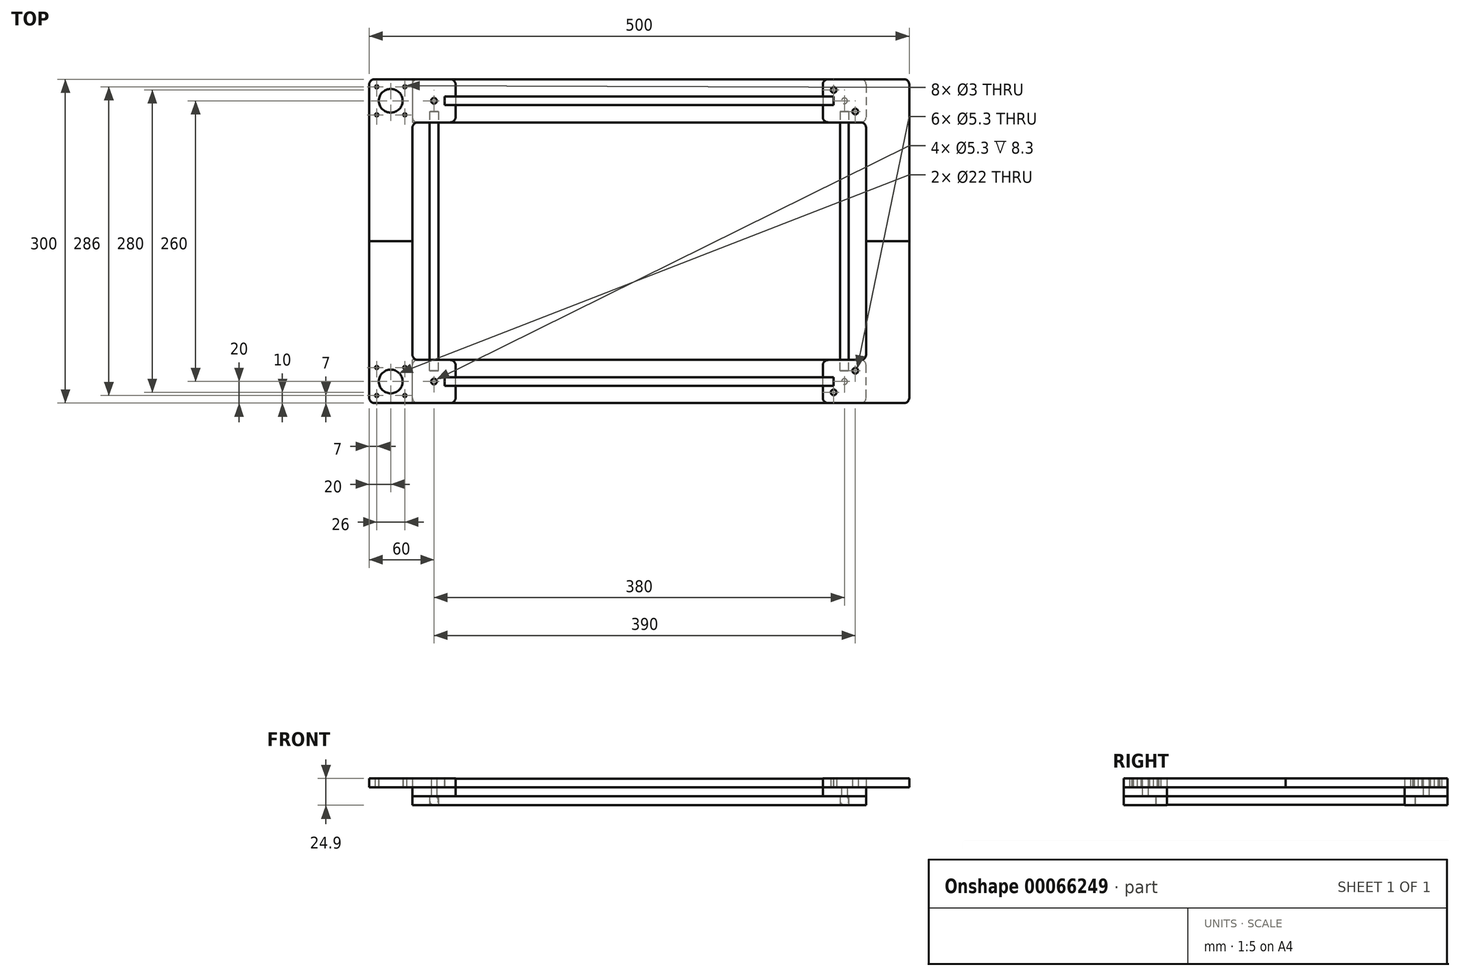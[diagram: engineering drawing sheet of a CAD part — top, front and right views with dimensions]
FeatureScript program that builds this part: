
annotation { "Feature Type Name" : "Feature", "Feature Type Description" : "" }
export const myFeature = defineFeature(function(context is Context, id is Id, definition is map)
    precondition{}
    {
        {
            assignVariable(context, id + "F0", {"name" : "thickness", "anyValue" : 8.3});
        }
        {
            var Q0;
            Q0=qCreatedBy(makeId("Top.planeOp"),FACE);
            var sketch = newSketch(context, id + "F1", { "sketchPlane" : qUnion([Q0])});
            skLineSegment(sketch, "E0.rect.bottom", {"start": v(170, -105) * mm, "end": v(-170, -105) * mm, "construction": true});
            skLineSegment(sketch, "E0.rect.top", {"start": v(170, 105) * mm, "end": v(-170, 105) * mm, "construction": true});
            skLineSegment(sketch, "E0.rect.left", {"start": v(170, -105) * mm, "end": v(170, 105) * mm, "construction": true});
            skLineSegment(sketch, "E0.rect.right", {"start": v(-170, -105) * mm, "end": v(-170, 105) * mm, "construction": true});
            skPoint(sketch, "E0.rect.middle", {"position": v(0, 0) * mm});
            skLineSegment(sketch, "E1.rect.bottom", {"start": v(250, -150) * mm, "end": v(-250, -150) * mm, "construction": true});
            skLineSegment(sketch, "E1.rect.top", {"start": v(250, 150) * mm, "end": v(-250, 150) * mm, "construction": true});
            skLineSegment(sketch, "E1.rect.left", {"start": v(250, -150) * mm, "end": v(250, 150) * mm, "construction": true});
            skLineSegment(sketch, "E1.rect.right", {"start": v(-250, -150) * mm, "end": v(-250, 150) * mm, "construction": true});
            skPoint(sketch, "E2.firstSnap0", {"position": v(170, 0) * mm});
            skLineSegment(sketch, "E2.bottom", {"start": v(170, 150) * mm, "end": v(250, 150) * mm, "construction": true});
            skLineSegment(sketch, "E2.top", {"start": v(170, -150) * mm, "end": v(250, -150) * mm, "construction": true});
            skLineSegment(sketch, "E2.left", {"start": v(170, 150) * mm, "end": v(170, -150) * mm, "construction": true});
            skLineSegment(sketch, "E2.right", {"start": v(250, 150) * mm, "end": v(250, -150) * mm, "construction": true});
            skLineSegment(sketch, "E3.bottom", {"start": v(-250, 150) * mm, "end": v(-170, 150) * mm, "construction": true});
            skLineSegment(sketch, "E3.top", {"start": v(-250, -150) * mm, "end": v(-170, -150) * mm, "construction": true});
            skLineSegment(sketch, "E3.left", {"start": v(-250, 150) * mm, "end": v(-250, -150) * mm, "construction": true});
            skLineSegment(sketch, "E3.right", {"start": v(-170, 150) * mm, "end": v(-170, -150) * mm, "construction": true});
            skPoint(sketch, "E4.rect.middle.positionSnap0", {"position": v(0, 105) * mm});
            skPoint(sketch, "E4.rect.centerSnap0", {"position": v(0, 105) * mm});
            skLineSegment(sketch, "E5.rect.bottom", {"start": v(-295.27, -46.95) * mm, "end": v(-355.57, -46.95) * mm, "construction": true});
            skLineSegment(sketch, "E5.rect.top", {"start": v(-295.27, 54.65) * mm, "end": v(-355.57, 54.65) * mm, "construction": true});
            skLineSegment(sketch, "E5.rect.left", {"start": v(-295.27, -46.95) * mm, "end": v(-295.27, 54.65) * mm, "construction": true});
            skLineSegment(sketch, "E5.rect.right", {"start": v(-355.57, -46.95) * mm, "end": v(-355.57, 54.65) * mm, "construction": true});
            skPoint(sketch, "E5.rect.middle.positionSnap0", {"position": v(-170, 0) * mm});
            skPoint(sketch, "E5.rect.centerSnap0", {"position": v(-170, 0) * mm});
            skLineSegment(sketch, "E6", {"start": v(-170, 0) * mm, "end": v(0, 0) * mm, "construction": true});
            skLineSegment(sketch, "E7.rect.top", {"start": v(-186, 0) * mm, "end": v(-194, 0) * mm, "construction": true});
            skLineSegment(sketch, "E7.rect.right", {"start": v(-194, 120) * mm, "end": v(-194, 0) * mm, "construction": true});
            skLineSegment(sketch, "E8", {"start": v(0, 0) * mm, "end": v(0, 105) * mm, "construction": true});
            skLineSegment(sketch, "E9.bottom", {"start": v(-180, 134) * mm, "end": v(0, 134) * mm, "construction": true});
            skLineSegment(sketch, "E9.top", {"start": v(-180, 126) * mm, "end": v(0, 126) * mm, "construction": true});
            skLineSegment(sketch, "E9.right", {"start": v(0, 134) * mm, "end": v(0, 126) * mm, "construction": true});
            skLineSegment(sketch, "E10.rect.bottom", {"start": v(-212.5, 112.5) * mm, "end": v(-247.5, 112.5) * mm, "construction": true});
            skLineSegment(sketch, "E10.rect.top", {"start": v(-212.5, 147.5) * mm, "end": v(-247.5, 147.5) * mm, "construction": true});
            skLineSegment(sketch, "E10.rect.left", {"start": v(-212.5, 112.5) * mm, "end": v(-212.5, 147.5) * mm, "construction": true});
            skLineSegment(sketch, "E10.rect.right", {"start": v(-247.5, 112.5) * mm, "end": v(-247.5, 147.5) * mm, "construction": true});
            skPoint(sketch, "E10.rect.middle", {"position": v(-230, 130) * mm});
            skLineSegment(sketch, "E11.rect.bottom", {"start": v(-217, 117) * mm, "end": v(-243, 117) * mm, "construction": true});
            skLineSegment(sketch, "E11.rect.top", {"start": v(-217, 143) * mm, "end": v(-243, 143) * mm, "construction": true});
            skLineSegment(sketch, "E11.rect.left", {"start": v(-217, 117) * mm, "end": v(-217, 143) * mm, "construction": true});
            skLineSegment(sketch, "E11.rect.right", {"start": v(-243, 117) * mm, "end": v(-243, 143) * mm, "construction": true});
            skCircle(sketch, "E12", {"center": v(-243, 143) * mm, "radius": 1.5 * mm, "construction": true});
            skCircle(sketch, "E13", {"center": v(-217, 143) * mm, "radius": 1.5 * mm, "construction": true});
            skCircle(sketch, "E14", {"center": v(-243, 117) * mm, "radius": 1.5 * mm, "construction": true});
            skCircle(sketch, "E15", {"center": v(-217, 117) * mm, "radius": 1.5 * mm, "construction": true});
            skLineSegment(sketch, "E16", {"start": v(-190, 130) * mm, "end": v(-180, 120) * mm, "construction": true});
            skLineSegment(sketch, "E17", {"start": v(-194, 120) * mm, "end": v(-186, 120) * mm, "construction": true});
            skLineSegment(sketch, "E18.trimOffspring", {"start": v(-186, 120) * mm, "end": v(-186, 0) * mm, "construction": true});
            skLineSegment(sketch, "E19", {"start": v(-180, 134) * mm, "end": v(-180, 126) * mm, "construction": true});
            skPoint(sketch, "E20", {"position": v(-190, 120) * mm});
            skPoint(sketch, "E21", {"position": v(-180, 130) * mm});
            skPoint(sketch, "E22", {"position": v(-190, 130) * mm});
            skLineSegment(sketch, "E23.top", {"start": v(-170, 110) * mm, "end": v(-210, 110) * mm, "construction": true});
            skLineSegment(sketch, "E23.left", {"start": v(-170, 150) * mm, "end": v(-170, 110) * mm, "construction": true});
            skLineSegment(sketch, "E23.right", {"start": v(-210, 150) * mm, "end": v(-210, 110) * mm, "construction": true});
            skLineSegment(sketch, "E24", {"start": v(-210, 150) * mm, "end": v(-170, 150) * mm});
            skLineSegment(sketch, "E25", {"start": v(-170, 110) * mm, "end": v(210, 110) * mm, "construction": true});
            skLineSegment(sketch, "E26", {"start": v(210, 110) * mm, "end": v(210, -110) * mm, "construction": true});
            skPoint(sketch, "E27.orphan", {"position": v(170, 110) * mm});
            skLineSegment(sketch, "E28.MirrorCS", {"start": v(-170, -110) * mm, "end": v(210, -110) * mm, "construction": true});
            skPoint(sketch, "E29.orphan", {"position": v(210, 0) * mm});
            skLineSegment(sketch, "E30", {"start": v(127, 105) * mm, "end": v(127, -105) * mm, "construction": true});
            skCircle(sketch, "E31", {"center": v(-190, 130) * mm, "radius": 2.65 * mm});
            skSolve(sketch);
        }
        {
            var Q0;
            Q0=qCreatedBy(makeId("Top.planeOp"),FACE);
            var sketch = newSketch(context, id + "F2", { "sketchPlane" : qUnion([Q0])});
            skLineSegment(sketch, "E32.0", {"start": v(-250, 0) * mm, "end": v(-250, 150) * mm});
            skLineSegment(sketch, "E33.0", {"start": v(-250, 150) * mm, "end": v(-170, 150) * mm});
            skLineSegment(sketch, "E34", {"start": v(-170, 150) * mm, "end": v(-170, 134) * mm});
            skLineSegment(sketch, "E35.0", {"start": v(-250, 0) * mm, "end": v(-210, 0) * mm});
            skLineSegment(sketch, "E36", {"start": v(-210, 110) * mm, "end": v(-210, 0) * mm});
            skLineSegment(sketch, "E37.trimOffspring", {"start": v(-170, 110) * mm, "end": v(-210, 110) * mm});
            skLineSegment(sketch, "E38.0", {"start": v(-180, 134) * mm, "end": v(-170, 134) * mm});
            skLineSegment(sketch, "E39.0", {"start": v(-180, 126) * mm, "end": v(-170, 126) * mm});
            skLineSegment(sketch, "E40.0", {"start": v(-180, 134) * mm, "end": v(-180, 126) * mm});
            skPoint(sketch, "E41.orphan", {"position": v(0, 134) * mm});
            skPoint(sketch, "E42.orphan", {"position": v(0, 126) * mm});
            skLineSegment(sketch, "E43.trimOffspring", {"start": v(-170, 126) * mm, "end": v(-170, 110) * mm});
            skLineSegment(sketch, "E44", {"start": v(0, 0) * mm, "end": v(0, 126) * mm, "construction": true});
            skLineSegment(sketch, "E45.MirrorCS", {"start": v(180, 126) * mm, "end": v(170, 126) * mm});
            skLineSegment(sketch, "E46.MirrorCS", {"start": v(180, 134) * mm, "end": v(180, 126) * mm});
            skLineSegment(sketch, "E47.MirrorCS", {"start": v(180, 134) * mm, "end": v(170, 134) * mm});
            skLineSegment(sketch, "E48.MirrorCS", {"start": v(170, 150) * mm, "end": v(170, 134) * mm});
            skLineSegment(sketch, "E49.MirrorCS", {"start": v(170, 126) * mm, "end": v(170, 110) * mm});
            skLineSegment(sketch, "E50.MirrorCS", {"start": v(170, 110) * mm, "end": v(210, 110) * mm});
            skLineSegment(sketch, "E51.MirrorCS", {"start": v(250, 150) * mm, "end": v(170, 150) * mm});
            skLineSegment(sketch, "E52.0", {"start": v(210, 110) * mm, "end": v(210, 0) * mm});
            skLineSegment(sketch, "E53", {"start": v(210, 0) * mm, "end": v(250, 0) * mm});
            skLineSegment(sketch, "E54.0", {"start": v(250, 150) * mm, "end": v(250, 0) * mm});
            skCircle(sketch, "E55.MirrorC", {"center": v(180, 120) * mm, "radius": 2.65 * mm, "construction": true});
            skCircle(sketch, "E56.MirrorC", {"center": v(200, 120) * mm, "radius": 2.65 * mm});
            skCircle(sketch, "E57.MirrorC", {"center": v(180, 140) * mm, "radius": 2.65 * mm});
            skCircle(sketch, "E58.0", {"center": v(-217, 143) * mm, "radius": 1.5 * mm});
            skCircle(sketch, "E59.0", {"center": v(-243, 143) * mm, "radius": 1.5 * mm});
            skCircle(sketch, "E60.0", {"center": v(-243, 117) * mm, "radius": 1.5 * mm});
            skCircle(sketch, "E61.0", {"center": v(-217, 117) * mm, "radius": 1.5 * mm});
            skCircle(sketch, "E62", {"center": v(-230, 130) * mm, "radius": 11 * mm});
            skCircle(sketch, "E63.0", {"center": v(-190, 130) * mm, "radius": 2.65 * mm});
            skSolve(sketch);
        }
        {
            var Q0;
            Q0=makeQuery(id+"F2.imprint","IMPRINT",FACE,{"disambiguationData":[TD([[makeQuery(id+"F2.imprint","IMPRINT",EDGE,{"derivedFrom":sQuery(id+"F2.wireOp",EDGE,"E32.0")}),-1.0]])]});
            var Q1;
            Q1=makeQuery(id+"F2.imprint","IMPRINT",FACE,{"disambiguationData":[TD([[makeQuery(id+"F2.imprint","IMPRINT",EDGE,{"derivedFrom":sQuery(id+"F2.wireOp",EDGE,"E45.MirrorCS")}),1.0]])]});
            extrude(context, id + "F3", {"entities" : qUnion([Q0, Q1]), "depth" : (getVariable(context, 'thickness') * 3) * mm, "hasSecondDirection" : true, "secondDirectionOppositeDirection" : false, "secondDirectionDepth" : (getVariable(context, 'thickness') * 2) * mm});
        }
        {
            var Q0;
            Q0=qCreatedBy(makeId("Top.planeOp"),FACE);
            var sketch = newSketch(context, id + "F4", { "sketchPlane" : qUnion([Q0])});
            skLineSegment(sketch, "E64.0", {"start": v(0, 150) * mm, "end": v(-210, 150) * mm});
            skLineSegment(sketch, "E65.0", {"start": v(-170, 110) * mm, "end": v(-170, -150) * mm});
            skLineSegment(sketch, "E66.0", {"start": v(-170, 110) * mm, "end": v(0, 110) * mm});
            skLineSegment(sketch, "E67.1", {"start": v(-210, 150) * mm, "end": v(-210, 110) * mm});
            skLineSegment(sketch, "E67.2", {"start": v(-170, 110) * mm, "end": v(-186, 110) * mm});
            skLineSegment(sketch, "E68.0", {"start": v(-194, 120) * mm, "end": v(-194, 110) * mm});
            skLineSegment(sketch, "E68.1", {"start": v(-186, 120) * mm, "end": v(-186, 110) * mm});
            skLineSegment(sketch, "E68.2", {"start": v(-194, 120) * mm, "end": v(-186, 120) * mm});
            skLineSegment(sketch, "E69.trimOffspring", {"start": v(-194, 110) * mm, "end": v(-210, 110) * mm});
            skPoint(sketch, "E70.orphan", {"position": v(-194, 0) * mm});
            skPoint(sketch, "E71.orphan", {"position": v(-186, 0) * mm});
            skLineSegment(sketch, "E72", {"start": v(0, 0) * mm, "end": v(0, 150) * mm});
            skSolve(sketch);
        }
        {
            var Q0;
            Q0 = qSketchRegion(id + "F4", true);
            extrude(context, id + "F5", {"entities" : qUnion([Q0]), "depth" : (getVariable(context, 'thickness')) * mm});
        }
        {
            var Q0;
            Q0=qCreatedBy(makeId("Top.planeOp"),FACE);
            var sketch = newSketch(context, id + "F6", { "sketchPlane" : qUnion([Q0])});
            skLineSegment(sketch, "E73.0", {"start": v(-170, 110) * mm, "end": v(-210, 110) * mm});
            skLineSegment(sketch, "E74.0", {"start": v(-170, 150) * mm, "end": v(-210, 150) * mm});
            skLineSegment(sketch, "E75.0", {"start": v(-210, 150) * mm, "end": v(-210, 110) * mm});
            skLineSegment(sketch, "E76.0", {"start": v(-170, 150) * mm, "end": v(-170, 110) * mm});
            skPoint(sketch, "E77.orphan", {"position": v(0, 150) * mm});
            skCircle(sketch, "E78.0", {"center": v(-190, 130) * mm, "radius": 2.65 * mm});
            skSolve(sketch);
        }
        {
            var Q0;
            Q0 = qSketchRegion(id + "F6", true);
            extrude(context, id + "F7", {"entities" : qUnion([Q0]), "depth" : (getVariable(context, 'thickness') * 2) * mm, "hasSecondDirection" : true, "secondDirectionOppositeDirection" : false, "secondDirectionDepth" : (getVariable(context, 'thickness')) * mm});
        }
        {
            var Q0;
            Q0=makeQuery(id+"F5.opExtrude","SWEPT_BODY",BODY,{"disambiguationData":[OSD([sQuery(id+"F4.wireOp",EDGE,"E64.0"),sQuery(id+"F4.wireOp",EDGE,"E66.0"),sQuery(id+"F4.wireOp",EDGE,"E67.1"),sQuery(id+"F4.wireOp",EDGE,"E67.2"),sQuery(id+"F4.wireOp",EDGE,"E68.0"),sQuery(id+"F4.wireOp",EDGE,"E68.1"),sQuery(id+"F4.wireOp",EDGE,"E68.2"),sQuery(id+"F4.wireOp",EDGE,"E69.trimOffspring"),sQuery(id+"F4.wireOp",EDGE,"E72")])]});
            var Q1;
            Q1=makeQuery(id+"F5.opExtrude","SWEPT_FACE",FACE,{"disambiguationData":[OSD([sQuery(id+"F4.wireOp",EDGE,"E72")])]});
            mirror(context, id + "F8", {"operationType" : NewBodyOperationType.ADD, "entities" : qUnion([Q0]), "mirrorPlane" : qUnion([Q1])});
        }
        {
            var Q0;
            Q0=makeQuery(id+"F7.opExtrude","SWEPT_BODY",BODY,{"disambiguationData":[OSD([sQuery(id+"F6.wireOp",EDGE,"E73.0"),sQuery(id+"F6.wireOp",EDGE,"E74.0"),sQuery(id+"F6.wireOp",EDGE,"E75.0"),sQuery(id+"F6.wireOp",EDGE,"E76.0")])]});
            var Q1;
            Q1=qCreatedBy(makeId("Right.planeOp"),FACE);
            mirror(context, id + "F9", {"entities" : qUnion([Q0]), "mirrorPlane" : qUnion([Q1])});
        }
        {
            var Q0;
            Q0=makeQuery(id+"F3.opExtrude","SWEPT_BODY",BODY,{"disambiguationData":[OSD([sQuery(id+"F2.wireOp",EDGE,"E32.0"),sQuery(id+"F2.wireOp",EDGE,"E33.0"),sQuery(id+"F2.wireOp",EDGE,"E34"),sQuery(id+"F2.wireOp",EDGE,"E35.0"),sQuery(id+"F2.wireOp",EDGE,"E36"),sQuery(id+"F2.wireOp",EDGE,"E37.trimOffspring"),sQuery(id+"F2.wireOp",EDGE,"E38.0"),sQuery(id+"F2.wireOp",EDGE,"E39.0"),sQuery(id+"F2.wireOp",EDGE,"E40.0"),sQuery(id+"F2.wireOp",EDGE,"E43.trimOffspring")])]});
            var Q1;
            Q1=makeQuery(id+"F7.opExtrude","SWEPT_BODY",BODY,{"disambiguationData":[OSD([sQuery(id+"F6.wireOp",EDGE,"E73.0"),sQuery(id+"F6.wireOp",EDGE,"E74.0"),sQuery(id+"F6.wireOp",EDGE,"E75.0"),sQuery(id+"F6.wireOp",EDGE,"E76.0")])]});
            var Q2;
            Q2=makeQuery(id+"F5.opExtrude","SWEPT_BODY",BODY,{"disambiguationData":[OSD([sQuery(id+"F4.wireOp",EDGE,"E64.0"),sQuery(id+"F4.wireOp",EDGE,"E66.0"),sQuery(id+"F4.wireOp",EDGE,"E67.1"),sQuery(id+"F4.wireOp",EDGE,"E67.2"),sQuery(id+"F4.wireOp",EDGE,"E68.0"),sQuery(id+"F4.wireOp",EDGE,"E68.1"),sQuery(id+"F4.wireOp",EDGE,"E68.2"),sQuery(id+"F4.wireOp",EDGE,"E69.trimOffspring"),sQuery(id+"F4.wireOp",EDGE,"E72")])]});
            var Q3;
            Q3=makeQuery(id+"F9.opPattern","COPY",BODY,{"derivedFrom":makeQuery(id+"F7.opExtrude","SWEPT_BODY",BODY,{"disambiguationData":[OSD([sQuery(id+"F6.wireOp",EDGE,"E73.0"),sQuery(id+"F6.wireOp",EDGE,"E74.0"),sQuery(id+"F6.wireOp",EDGE,"E75.0"),sQuery(id+"F6.wireOp",EDGE,"E76.0")])]}),"instanceName":"1"});
            var Q4;
            Q4=makeQuery(id+"F3.opExtrude","SWEPT_BODY",BODY,{"disambiguationData":[OSD([sQuery(id+"F2.wireOp",EDGE,"E45.MirrorCS"),sQuery(id+"F2.wireOp",EDGE,"E46.MirrorCS"),sQuery(id+"F2.wireOp",EDGE,"E47.MirrorCS"),sQuery(id+"F2.wireOp",EDGE,"E48.MirrorCS"),sQuery(id+"F2.wireOp",EDGE,"E49.MirrorCS"),sQuery(id+"F2.wireOp",EDGE,"E50.MirrorCS"),sQuery(id+"F2.wireOp",EDGE,"E51.MirrorCS"),sQuery(id+"F2.wireOp",EDGE,"E52.0"),sQuery(id+"F2.wireOp",EDGE,"E53"),sQuery(id+"F2.wireOp",EDGE,"E54.0")])]});
            var Q5;
            Q5=qCreatedBy(makeId("Front.planeOp"),FACE);
            mirror(context, id + "F10", {"entities" : qUnion([Q0, Q1, Q2, Q3, Q4]), "mirrorPlane" : qUnion([Q5])});
        }
        {
            var Q0;
            Q0=makeQuery(id+"F5.opExtrude","SWEPT_FACE",FACE,{"disambiguationData":[OSD([sQuery(id+"F4.wireOp",EDGE,"E68.2")])]});
            var sketch = newSketch(context, id + "F11", { "sketchPlane" : qUnion([Q0])});
            skCircle(sketch, "E79", {"center": v(-190, 4.3) * mm, "radius": 4 * mm});
            skPoint(sketch, "E80", {"position": v(-190, 8.3) * mm});
            skSolve(sketch);
        }
        {
            var Q0;
            Q0 = qSketchRegion(id + "F11", true);
            var Q1;
            Q1=makeQuery(id+"F10.opPattern","COPY",FACE,{"derivedFrom":makeQuery(id+"F5.opExtrude","SWEPT_FACE",FACE,{"disambiguationData":[OSD([sQuery(id+"F4.wireOp",EDGE,"E68.2")])]}),"instanceName":"1"});
            extrude(context, id + "F12", {"entities" : qUnion([Q0]), "endBound" : BoundingType.UP_TO_SURFACE, "endBoundEntityFace" : qUnion([Q1]), "depth" : 324.03 * mm});
        }
        {
            var Q0;
            Q0=makeQuery(id+"F3.opExtrude","SWEPT_FACE",FACE,{"disambiguationData":[OSD([sQuery(id+"F2.wireOp",EDGE,"E40.0")])]});
            var sketch = newSketch(context, id + "F13", { "sketchPlane" : qUnion([Q0])});
            skCircle(sketch, "E81", {"center": v(130, 20.6) * mm, "radius": 4 * mm});
            skPoint(sketch, "E82", {"position": v(130, 16.6) * mm});
            skSolve(sketch);
        }
        {
            var Q0;
            Q0 = qSketchRegion(id + "F13", true);
            var Q1;
            Q1=makeQuery(id+"F3.opExtrude","SWEPT_FACE",FACE,{"disambiguationData":[OSD([sQuery(id+"F2.wireOp",EDGE,"E46.MirrorCS")])]});
            extrude(context, id + "F14", {"entities" : qUnion([Q0]), "endBound" : BoundingType.UP_TO_SURFACE, "endBoundEntityFace" : qUnion([Q1]), "depth" : 25 * mm});
        }
        {
            var Q0;
            Q0=makeQuery(id+"F12.opExtrude","SWEPT_BODY",BODY,{"disambiguationData":[OSD([sQuery(id+"F11.wireOp",EDGE,"E79")])]});
            var Q1;
            Q1=qCreatedBy(makeId("Right.planeOp"),FACE);
            mirror(context, id + "F15", {"entities" : qUnion([Q0]), "mirrorPlane" : qUnion([Q1])});
        }
        {
            var Q0;
            Q0=makeQuery(id+"F14.opExtrude","SWEPT_BODY",BODY,{"disambiguationData":[OSD([sQuery(id+"F13.wireOp",EDGE,"E81")])]});
            var Q1;
            Q1=qCreatedBy(makeId("Front.planeOp"),FACE);
            mirror(context, id + "F16", {"entities" : qUnion([Q0]), "mirrorPlane" : qUnion([Q1])});
        }
        {
            var Q0;
            Q0=makeQuery(id+"F10.opPattern","COPY",EDGE,{"derivedFrom":makeQuery(id+"F3.opExtrude","SWEPT_EDGE",EDGE,{"disambiguationData":[OSD([sQuery(id+"F2.wireOp",EDGE,"E51.MirrorCS"),sQuery(id+"F2.wireOp",EDGE,"E54.0")])]}),"instanceName":"1"});
            var Q1;
            Q1=makeQuery(id+"F3.opExtrude","SWEPT_EDGE",EDGE,{"disambiguationData":[OSD([sQuery(id+"F2.wireOp",EDGE,"E51.MirrorCS"),sQuery(id+"F2.wireOp",EDGE,"E54.0")])]});
            var Q2;
            Q2=makeQuery(id+"F10.opPattern","COPY",EDGE,{"derivedFrom":makeQuery(id+"F3.opExtrude","SWEPT_EDGE",EDGE,{"disambiguationData":[OSD([sQuery(id+"F2.wireOp",EDGE,"E32.0"),sQuery(id+"F2.wireOp",EDGE,"E33.0")])]}),"instanceName":"1"});
            var Q3;
            Q3=makeQuery(id+"F3.opExtrude","SWEPT_EDGE",EDGE,{"disambiguationData":[OSD([sQuery(id+"F2.wireOp",EDGE,"E32.0"),sQuery(id+"F2.wireOp",EDGE,"E33.0")])]});
            var Q4;
            Q4=makeQuery(id+"F3.opExtrude","SWEPT_EDGE",EDGE,{"disambiguationData":[OSD([sQuery(id+"F2.wireOp",EDGE,"E33.0"),sQuery(id+"F2.wireOp",EDGE,"E34")])]});
            var Q5;
            Q5=makeQuery(id+"F3.opExtrude","SWEPT_EDGE",EDGE,{"disambiguationData":[OSD([sQuery(id+"F2.wireOp",EDGE,"E37.trimOffspring"),sQuery(id+"F2.wireOp",EDGE,"E43.trimOffspring")])]});
            var Q6;
            Q6=makeQuery(id+"F7.opExtrude","SWEPT_EDGE",EDGE,{"disambiguationData":[OSD([sQuery(id+"F6.wireOp",EDGE,"E73.0"),sQuery(id+"F6.wireOp",EDGE,"E76.0")])]});
            var Q7;
            Q7=makeQuery(id+"F7.opExtrude","SWEPT_EDGE",EDGE,{"disambiguationData":[OSD([sQuery(id+"F6.wireOp",EDGE,"E74.0"),sQuery(id+"F6.wireOp",EDGE,"E76.0")])]});
            var Q8;
            Q8=makeQuery(id+"F7.opExtrude","SWEPT_EDGE",EDGE,{"disambiguationData":[OSD([sQuery(id+"F6.wireOp",EDGE,"E74.0"),sQuery(id+"F6.wireOp",EDGE,"E75.0")])]});
            var Q9;
            Q9=makeQuery(id+"F5.opExtrude","SWEPT_EDGE",EDGE,{"disambiguationData":[OSD([sQuery(id+"F4.wireOp",EDGE,"E64.0"),sQuery(id+"F4.wireOp",EDGE,"E67.1")])]});
            var Q10;
            Q10=makeQuery(id+"F7.opExtrude","SWEPT_EDGE",EDGE,{"disambiguationData":[OSD([sQuery(id+"F6.wireOp",EDGE,"E73.0"),sQuery(id+"F6.wireOp",EDGE,"E75.0")])]});
            var Q11;
            Q11=makeQuery(id+"F5.opExtrude","SWEPT_EDGE",EDGE,{"disambiguationData":[OSD([sQuery(id+"F4.wireOp",EDGE,"E67.1"),sQuery(id+"F4.wireOp",EDGE,"E69.trimOffspring")])]});
            var Q12;
            Q12=makeQuery(id+"F3.opExtrude","SWEPT_EDGE",EDGE,{"disambiguationData":[OSD([sQuery(id+"F2.wireOp",EDGE,"E48.MirrorCS"),sQuery(id+"F2.wireOp",EDGE,"E51.MirrorCS")])]});
            var Q13;
            Q13=makeQuery(id+"F9.opPattern","COPY",EDGE,{"derivedFrom":makeQuery(id+"F7.opExtrude","SWEPT_EDGE",EDGE,{"disambiguationData":[OSD([sQuery(id+"F6.wireOp",EDGE,"E74.0"),sQuery(id+"F6.wireOp",EDGE,"E76.0")])]}),"instanceName":"1"});
            var Q14;
            Q14=makeQuery(id+"F9.opPattern","COPY",EDGE,{"derivedFrom":makeQuery(id+"F7.opExtrude","SWEPT_EDGE",EDGE,{"disambiguationData":[OSD([sQuery(id+"F6.wireOp",EDGE,"E74.0"),sQuery(id+"F6.wireOp",EDGE,"E75.0")])]}),"instanceName":"1"});
            var Q15;
            Q15=makeQuery(id+"F8.opPattern","COPY",EDGE,{"derivedFrom":makeQuery(id+"F5.opExtrude","SWEPT_EDGE",EDGE,{"disambiguationData":[OSD([sQuery(id+"F4.wireOp",EDGE,"E64.0"),sQuery(id+"F4.wireOp",EDGE,"E67.1")])]}),"instanceName":"1"});
            var Q16;
            Q16=makeQuery(id+"F3.opExtrude","SWEPT_EDGE",EDGE,{"disambiguationData":[OSD([sQuery(id+"F2.wireOp",EDGE,"E49.MirrorCS"),sQuery(id+"F2.wireOp",EDGE,"E50.MirrorCS")])]});
            var Q17;
            Q17=makeQuery(id+"F9.opPattern","COPY",EDGE,{"derivedFrom":makeQuery(id+"F7.opExtrude","SWEPT_EDGE",EDGE,{"disambiguationData":[OSD([sQuery(id+"F6.wireOp",EDGE,"E73.0"),sQuery(id+"F6.wireOp",EDGE,"E76.0")])]}),"instanceName":"1"});
            var Q18;
            Q18=makeQuery(id+"F8.opPattern","COPY",EDGE,{"derivedFrom":makeQuery(id+"F5.opExtrude","SWEPT_EDGE",EDGE,{"disambiguationData":[OSD([sQuery(id+"F4.wireOp",EDGE,"E67.1"),sQuery(id+"F4.wireOp",EDGE,"E69.trimOffspring")])]}),"instanceName":"1"});
            var Q19;
            Q19=makeQuery(id+"F9.opPattern","COPY",EDGE,{"derivedFrom":makeQuery(id+"F7.opExtrude","SWEPT_EDGE",EDGE,{"disambiguationData":[OSD([sQuery(id+"F6.wireOp",EDGE,"E73.0"),sQuery(id+"F6.wireOp",EDGE,"E75.0")])]}),"instanceName":"1"});
            var Q20;
            Q20=makeQuery(id+"F10.opPattern","COPY",EDGE,{"derivedFrom":makeQuery(id+"F8.opPattern","COPY",EDGE,{"derivedFrom":makeQuery(id+"F5.opExtrude","SWEPT_EDGE",EDGE,{"disambiguationData":[OSD([sQuery(id+"F4.wireOp",EDGE,"E64.0"),sQuery(id+"F4.wireOp",EDGE,"E67.1")])]}),"instanceName":"1"}),"instanceName":"1"});
            var Q21;
            Q21=makeQuery(id+"F10.opPattern","COPY",EDGE,{"derivedFrom":makeQuery(id+"F9.opPattern","COPY",EDGE,{"derivedFrom":makeQuery(id+"F7.opExtrude","SWEPT_EDGE",EDGE,{"disambiguationData":[OSD([sQuery(id+"F6.wireOp",EDGE,"E74.0"),sQuery(id+"F6.wireOp",EDGE,"E75.0")])]}),"instanceName":"1"}),"instanceName":"1"});
            var Q22;
            Q22=makeQuery(id+"F10.opPattern","COPY",EDGE,{"derivedFrom":makeQuery(id+"F8.opPattern","COPY",EDGE,{"derivedFrom":makeQuery(id+"F5.opExtrude","SWEPT_EDGE",EDGE,{"disambiguationData":[OSD([sQuery(id+"F4.wireOp",EDGE,"E67.1"),sQuery(id+"F4.wireOp",EDGE,"E69.trimOffspring")])]}),"instanceName":"1"}),"instanceName":"1"});
            var Q23;
            Q23=makeQuery(id+"F10.opPattern","COPY",EDGE,{"derivedFrom":makeQuery(id+"F9.opPattern","COPY",EDGE,{"derivedFrom":makeQuery(id+"F7.opExtrude","SWEPT_EDGE",EDGE,{"disambiguationData":[OSD([sQuery(id+"F6.wireOp",EDGE,"E73.0"),sQuery(id+"F6.wireOp",EDGE,"E75.0")])]}),"instanceName":"1"}),"instanceName":"1"});
            var Q24;
            Q24=makeQuery(id+"F10.opPattern","COPY",EDGE,{"derivedFrom":makeQuery(id+"F3.opExtrude","SWEPT_EDGE",EDGE,{"disambiguationData":[OSD([sQuery(id+"F2.wireOp",EDGE,"E48.MirrorCS"),sQuery(id+"F2.wireOp",EDGE,"E51.MirrorCS")])]}),"instanceName":"1"});
            var Q25;
            Q25=makeQuery(id+"F10.opPattern","COPY",EDGE,{"derivedFrom":makeQuery(id+"F9.opPattern","COPY",EDGE,{"derivedFrom":makeQuery(id+"F7.opExtrude","SWEPT_EDGE",EDGE,{"disambiguationData":[OSD([sQuery(id+"F6.wireOp",EDGE,"E74.0"),sQuery(id+"F6.wireOp",EDGE,"E76.0")])]}),"instanceName":"1"}),"instanceName":"1"});
            var Q26;
            Q26=makeQuery(id+"F10.opPattern","COPY",EDGE,{"derivedFrom":makeQuery(id+"F3.opExtrude","SWEPT_EDGE",EDGE,{"disambiguationData":[OSD([sQuery(id+"F2.wireOp",EDGE,"E49.MirrorCS"),sQuery(id+"F2.wireOp",EDGE,"E50.MirrorCS")])]}),"instanceName":"1"});
            var Q27;
            Q27=makeQuery(id+"F10.opPattern","COPY",EDGE,{"derivedFrom":makeQuery(id+"F9.opPattern","COPY",EDGE,{"derivedFrom":makeQuery(id+"F7.opExtrude","SWEPT_EDGE",EDGE,{"disambiguationData":[OSD([sQuery(id+"F6.wireOp",EDGE,"E73.0"),sQuery(id+"F6.wireOp",EDGE,"E76.0")])]}),"instanceName":"1"}),"instanceName":"1"});
            var Q28;
            Q28=makeQuery(id+"F10.opPattern","COPY",EDGE,{"derivedFrom":makeQuery(id+"F3.opExtrude","SWEPT_EDGE",EDGE,{"disambiguationData":[OSD([sQuery(id+"F2.wireOp",EDGE,"E37.trimOffspring"),sQuery(id+"F2.wireOp",EDGE,"E43.trimOffspring")])]}),"instanceName":"1"});
            var Q29;
            Q29=makeQuery(id+"F10.opPattern","COPY",EDGE,{"derivedFrom":makeQuery(id+"F7.opExtrude","SWEPT_EDGE",EDGE,{"disambiguationData":[OSD([sQuery(id+"F6.wireOp",EDGE,"E73.0"),sQuery(id+"F6.wireOp",EDGE,"E76.0")])]}),"instanceName":"1"});
            var Q30;
            Q30=makeQuery(id+"F10.opPattern","COPY",EDGE,{"derivedFrom":makeQuery(id+"F7.opExtrude","SWEPT_EDGE",EDGE,{"disambiguationData":[OSD([sQuery(id+"F6.wireOp",EDGE,"E74.0"),sQuery(id+"F6.wireOp",EDGE,"E76.0")])]}),"instanceName":"1"});
            var Q31;
            Q31=makeQuery(id+"F10.opPattern","COPY",EDGE,{"derivedFrom":makeQuery(id+"F3.opExtrude","SWEPT_EDGE",EDGE,{"disambiguationData":[OSD([sQuery(id+"F2.wireOp",EDGE,"E33.0"),sQuery(id+"F2.wireOp",EDGE,"E34")])]}),"instanceName":"1"});
            var Q32;
            Q32=makeQuery(id+"F10.opPattern","COPY",EDGE,{"derivedFrom":makeQuery(id+"F7.opExtrude","SWEPT_EDGE",EDGE,{"disambiguationData":[OSD([sQuery(id+"F6.wireOp",EDGE,"E74.0"),sQuery(id+"F6.wireOp",EDGE,"E75.0")])]}),"instanceName":"1"});
            var Q33;
            Q33=makeQuery(id+"F10.opPattern","COPY",EDGE,{"derivedFrom":makeQuery(id+"F5.opExtrude","SWEPT_EDGE",EDGE,{"disambiguationData":[OSD([sQuery(id+"F4.wireOp",EDGE,"E64.0"),sQuery(id+"F4.wireOp",EDGE,"E67.1")])]}),"instanceName":"1"});
            var Q34;
            Q34=makeQuery(id+"F10.opPattern","COPY",EDGE,{"derivedFrom":makeQuery(id+"F7.opExtrude","SWEPT_EDGE",EDGE,{"disambiguationData":[OSD([sQuery(id+"F6.wireOp",EDGE,"E73.0"),sQuery(id+"F6.wireOp",EDGE,"E75.0")])]}),"instanceName":"1"});
            var Q35;
            Q35=makeQuery(id+"F10.opPattern","COPY",EDGE,{"derivedFrom":makeQuery(id+"F5.opExtrude","SWEPT_EDGE",EDGE,{"disambiguationData":[OSD([sQuery(id+"F4.wireOp",EDGE,"E67.1"),sQuery(id+"F4.wireOp",EDGE,"E69.trimOffspring")])]}),"instanceName":"1"});
            var Q36;
            Q36=makeQuery(id+"F10.opPattern","COPY",EDGE,{"derivedFrom":makeQuery(id+"F3.opExtrude","SWEPT_EDGE",EDGE,{"disambiguationData":[OSD([sQuery(id+"F2.wireOp",EDGE,"E50.MirrorCS"),sQuery(id+"F2.wireOp",EDGE,"E52.0")])]}),"instanceName":"1"});
            var Q37;
            Q37=makeQuery(id+"F10.opPattern","COPY",EDGE,{"derivedFrom":makeQuery(id+"F3.opExtrude","SWEPT_EDGE",EDGE,{"disambiguationData":[OSD([sQuery(id+"F2.wireOp",EDGE,"E36"),sQuery(id+"F2.wireOp",EDGE,"E37.trimOffspring")])]}),"instanceName":"1"});
            var Q38;
            Q38=makeQuery(id+"F3.opExtrude","SWEPT_EDGE",EDGE,{"disambiguationData":[OSD([sQuery(id+"F2.wireOp",EDGE,"E36"),sQuery(id+"F2.wireOp",EDGE,"E37.trimOffspring")])]});
            var Q39;
            Q39=makeQuery(id+"F3.opExtrude","SWEPT_EDGE",EDGE,{"disambiguationData":[OSD([sQuery(id+"F2.wireOp",EDGE,"E50.MirrorCS"),sQuery(id+"F2.wireOp",EDGE,"E52.0")])]});
            fillet(context, id + "F17", {"entities" : qUnion([Q0, Q1, Q2, Q3, Q4, Q5, Q6, Q7, Q8, Q9, Q10, Q11, Q12, Q13, Q14, Q15, Q16, Q17, Q18, Q19, Q20, Q21, Q22, Q23, Q24, Q25, Q26, Q27, Q28, Q29, Q30, Q31, Q32, Q33, Q34, Q35, Q36, Q37, Q38, Q39]), "radius" : 5 * mm, "tangentPropagation" : true, "allowEdgeOverflow" : false});
        }
    });
